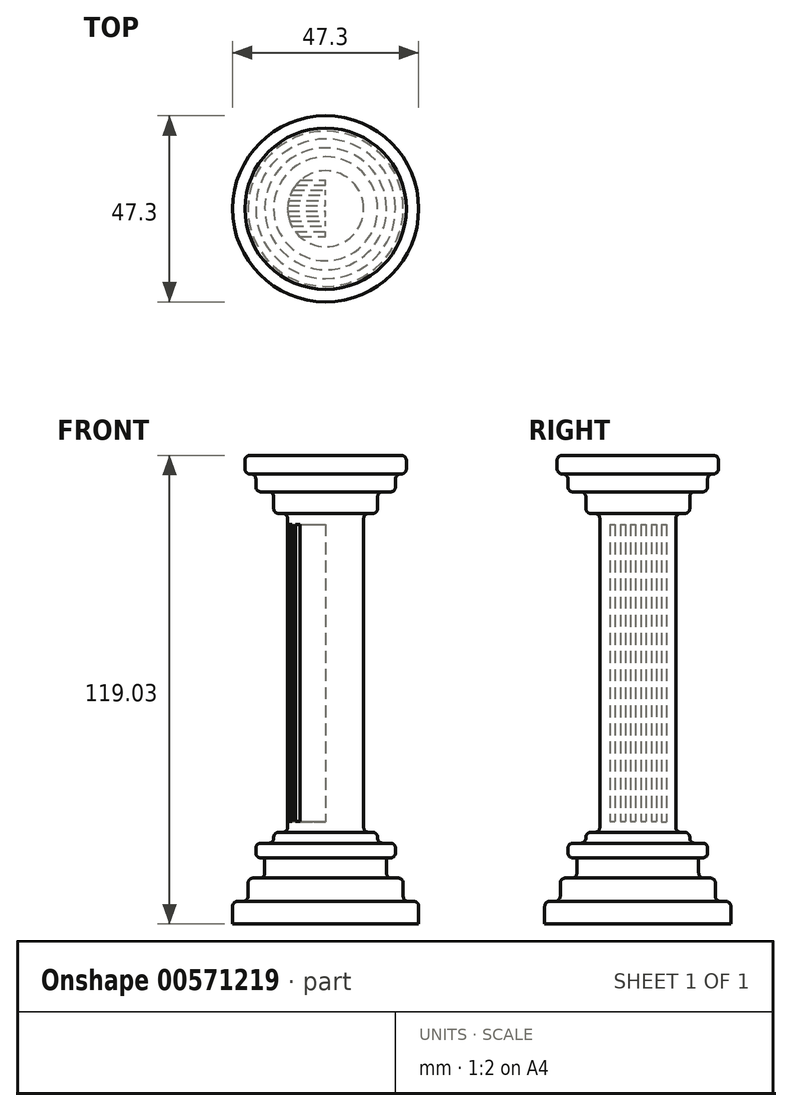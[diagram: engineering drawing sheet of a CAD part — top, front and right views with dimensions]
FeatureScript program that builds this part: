
annotation { "Feature Type Name" : "Feature", "Feature Type Description" : "" }
export const myFeature = defineFeature(function(context is Context, id is Id, definition is map)
    precondition{}
    {
        {
            var Q0;
            Q0=qCreatedBy(makeId("Right.planeOp"),FACE);
            var sketch = newSketch(context, id + "F0", { "sketchPlane" : qUnion([Q0])});
            skLineSegment(sketch, "E0", {"start": v(0, -56.36) * mm, "end": v(0, 43.27) * mm});
            skLineSegment(sketch, "E1", {"start": v(-12.7, 55.97) * mm, "end": v(-19.23, 55.97) * mm});
            skLineSegment(sketch, "E2", {"start": v(-20.5, 54.7) * mm, "end": v(-20.5, 52.5) * mm});
            skLineSegment(sketch, "E3", {"start": v(-19.23, 51.24) * mm, "end": v(-19, 51.24) * mm});
            skLineSegment(sketch, "E4", {"start": v(-17.74, 49.97) * mm, "end": v(-17.74, 47.98) * mm});
            skLineSegment(sketch, "E5", {"start": v(-16.47, 46.7) * mm, "end": v(-14.47, 46.7) * mm});
            skLineSegment(sketch, "E6", {"start": v(-13.2, 45.44) * mm, "end": v(-13.2, 42.46) * mm});
            skLineSegment(sketch, "E7", {"start": v(-11.93, 41.19) * mm, "end": v(-10.93, 41.19) * mm});
            skLineSegment(sketch, "E8", {"start": v(-9.66, 39.92) * mm, "end": v(-9.66, -38.54) * mm});
            skLineSegment(sketch, "E9", {"start": v(-10.93, -39.8) * mm, "end": v(-11.93, -39.8) * mm});
            skLineSegment(sketch, "E10", {"start": v(-13.2, -41.08) * mm, "end": v(-13.2, -41.3) * mm});
            skLineSegment(sketch, "E11", {"start": v(-14.47, -42.57) * mm, "end": v(-16.47, -42.57) * mm});
            skLineSegment(sketch, "E12", {"start": v(-17.74, -43.84) * mm, "end": v(-17.74, -45.04) * mm});
            skLineSegment(sketch, "E13", {"start": v(-16.47, -46.31) * mm, "end": v(-15.47, -46.31) * mm});
            skPoint(sketch, "E13.endSnap0", {"position": v(-15.47, -42.57) * mm});
            skLineSegment(sketch, "E14", {"start": v(-15.47, -46.31) * mm, "end": v(-15.47, -50.17) * mm});
            skLineSegment(sketch, "E15", {"start": v(-16.74, -51.44) * mm, "end": v(-18.44, -51.44) * mm});
            skLineSegment(sketch, "E16", {"start": v(-19.7, -52.7) * mm, "end": v(-19.7, -56.08) * mm});
            skLineSegment(sketch, "E17", {"start": v(-20.98, -57.35) * mm, "end": v(-22.38, -57.35) * mm});
            skLineSegment(sketch, "E18", {"start": v(-23.65, -58.62) * mm, "end": v(-23.65, -63.06) * mm});
            skLineSegment(sketch, "E19", {"start": v(-23.65, -63.06) * mm, "end": v(0, -63.06) * mm});
            skLineSegment(sketch, "E20", {"start": v(0, -63.06) * mm, "end": v(0, -56.36) * mm});
            skPoint(sketch, "E21.visualSharp", {"position": v(0, 55.97) * mm});
            skPoint(sketch, "E22.visualSharp", {"position": v(-20.5, 55.97) * mm});
            skArc(sketch, "E22.filletArc", {"start": v(-19.23, 55.97) * mm, "mid": v(-20.12, 55.6) * mm, "end": v(-20.5, 54.7) * mm});
            skPoint(sketch, "E23.visualSharp", {"position": v(-20.5, 51.24) * mm});
            skArc(sketch, "E23.filletArc", {"start": v(-20.5, 52.5) * mm, "mid": v(-20.12, 51.6) * mm, "end": v(-19.23, 51.24) * mm});
            skPoint(sketch, "E24.visualSharp", {"position": v(-17.74, 51.24) * mm});
            skArc(sketch, "E24.filletArc", {"start": v(-17.74, 49.97) * mm, "mid": v(-18.1, 50.87) * mm, "end": v(-19, 51.24) * mm});
            skPoint(sketch, "E25.visualSharp", {"position": v(-17.74, 46.7) * mm});
            skArc(sketch, "E25.filletArc", {"start": v(-17.74, 47.98) * mm, "mid": v(-17.36, 47.08) * mm, "end": v(-16.47, 46.7) * mm});
            skPoint(sketch, "E26.visualSharp", {"position": v(-13.2, 46.7) * mm});
            skArc(sketch, "E26.filletArc", {"start": v(-13.2, 45.44) * mm, "mid": v(-13.58, 46.33) * mm, "end": v(-14.47, 46.7) * mm});
            skPoint(sketch, "E27.visualSharp", {"position": v(-13.2, 41.19) * mm});
            skArc(sketch, "E27.filletArc", {"start": v(-13.2, 42.46) * mm, "mid": v(-12.83, 41.56) * mm, "end": v(-11.93, 41.19) * mm});
            skPoint(sketch, "E28.visualSharp", {"position": v(-9.66, 41.19) * mm});
            skArc(sketch, "E28.filletArc", {"start": v(-9.66, 39.92) * mm, "mid": v(-10.03, 40.82) * mm, "end": v(-10.93, 41.19) * mm});
            skPoint(sketch, "E29.visualSharp", {"position": v(-9.66, -39.8) * mm});
            skArc(sketch, "E29.filletArc", {"start": v(-10.93, -39.8) * mm, "mid": v(-10.03, -39.44) * mm, "end": v(-9.66, -38.54) * mm});
            skPoint(sketch, "E30.visualSharp", {"position": v(-13.2, -39.8) * mm});
            skArc(sketch, "E30.filletArc", {"start": v(-11.93, -39.8) * mm, "mid": v(-12.83, -40.18) * mm, "end": v(-13.2, -41.08) * mm});
            skPoint(sketch, "E31.visualSharp", {"position": v(-13.2, -42.57) * mm});
            skArc(sketch, "E31.filletArc", {"start": v(-14.47, -42.57) * mm, "mid": v(-13.58, -42.2) * mm, "end": v(-13.2, -41.3) * mm});
            skPoint(sketch, "E32.visualSharp", {"position": v(-17.74, -42.57) * mm});
            skArc(sketch, "E32.filletArc", {"start": v(-16.47, -42.57) * mm, "mid": v(-17.36, -42.94) * mm, "end": v(-17.74, -43.84) * mm});
            skPoint(sketch, "E33.visualSharp", {"position": v(-17.74, -46.31) * mm});
            skArc(sketch, "E33.filletArc", {"start": v(-17.74, -45.04) * mm, "mid": v(-17.36, -45.94) * mm, "end": v(-16.47, -46.31) * mm});
            skPoint(sketch, "E34.visualSharp", {"position": v(-15.47, -51.44) * mm});
            skArc(sketch, "E34.filletArc", {"start": v(-16.74, -51.44) * mm, "mid": v(-15.84, -51.06) * mm, "end": v(-15.47, -50.17) * mm});
            skPoint(sketch, "E35.visualSharp", {"position": v(-19.7, -51.44) * mm});
            skArc(sketch, "E35.filletArc", {"start": v(-18.44, -51.44) * mm, "mid": v(-19.33, -51.8) * mm, "end": v(-19.7, -52.7) * mm});
            skPoint(sketch, "E36.visualSharp", {"position": v(-19.7, -57.35) * mm});
            skArc(sketch, "E36.filletArc", {"start": v(-20.98, -57.35) * mm, "mid": v(-20.08, -56.98) * mm, "end": v(-19.7, -56.08) * mm});
            skPoint(sketch, "E37.visualSharp", {"position": v(-23.65, -57.35) * mm});
            skArc(sketch, "E37.filletArc", {"start": v(-22.38, -57.35) * mm, "mid": v(-23.28, -57.72) * mm, "end": v(-23.65, -58.62) * mm});
            skLineSegment(sketch, "E38", {"start": v(-12.7, 55.97) * mm, "end": v(0, 55.97) * mm});
            skLineSegment(sketch, "E39", {"start": v(0, 43.27) * mm, "end": v(0, 55.97) * mm});
            skSolve(sketch);
        }
        {
            var Q0;
            Q0=makeQuery(id+"F0.imprint","IMPRINT",FACE,{"disambiguationData":[TD([[makeQuery(id+"F0.imprint","IMPRINT",EDGE,{"derivedFrom":sQuery(id+"F0.wireOp",EDGE,"E0")}),1.0]])]});
            var Q1;
            Q1=sQuery(id+"F0.wireOp",EDGE,"E0");
            revolve(context, id + "F1", {"entities" : qUnion([Q0]), "axis" : qUnion([Q1]), "revolveType" : RevolveType.FULL});
        }
        {
            var Q0;
            Q0=qCreatedBy(makeId("Right.planeOp"),FACE);
            var sketch = newSketch(context, id + "F2", { "sketchPlane" : qUnion([Q0])});
            skLineSegment(sketch, "E40.bottom", {"start": v(-7.1, 38.43) * mm, "end": v(-5.8, 38.43) * mm});
            skLineSegment(sketch, "E40.top", {"start": v(-7.1, -37.05) * mm, "end": v(-5.8, -37.05) * mm});
            skLineSegment(sketch, "E40.left", {"start": v(-7.1, 38.43) * mm, "end": v(-7.1, -37.05) * mm});
            skLineSegment(sketch, "E40.right", {"start": v(-5.8, 38.43) * mm, "end": v(-5.8, -37.05) * mm});
            skLineSegment(sketch, "E41.bottom", {"start": v(-4.38, 38.43) * mm, "end": v(-3.1, 38.43) * mm});
            skLineSegment(sketch, "E41.top", {"start": v(-4.38, -37.08) * mm, "end": v(-3.1, -37.08) * mm});
            skLineSegment(sketch, "E41.left", {"start": v(-4.38, 38.43) * mm, "end": v(-4.38, -37.08) * mm});
            skLineSegment(sketch, "E41.right", {"start": v(-3.1, 38.43) * mm, "end": v(-3.1, -37.08) * mm});
            skLineSegment(sketch, "E42.bottom", {"start": v(-1.87, 38.42) * mm, "end": v(-0.59, 38.42) * mm});
            skLineSegment(sketch, "E42.top", {"start": v(-1.87, -37.07) * mm, "end": v(-0.59, -37.07) * mm});
            skLineSegment(sketch, "E42.left", {"start": v(-1.87, 38.42) * mm, "end": v(-1.87, -37.07) * mm});
            skLineSegment(sketch, "E42.right", {"start": v(-0.59, 38.42) * mm, "end": v(-0.59, -37.07) * mm});
            skLineSegment(sketch, "E43.bottom", {"start": v(0.78, 38.42) * mm, "end": v(2.07, 38.42) * mm});
            skLineSegment(sketch, "E43.top", {"start": v(0.78, -37.08) * mm, "end": v(2.07, -37.08) * mm});
            skLineSegment(sketch, "E43.left", {"start": v(0.78, 38.42) * mm, "end": v(0.78, -37.08) * mm});
            skLineSegment(sketch, "E43.right", {"start": v(2.07, 38.42) * mm, "end": v(2.07, -37.08) * mm});
            skLineSegment(sketch, "E44.bottom", {"start": v(3.49, 38.45) * mm, "end": v(4.77, 38.45) * mm});
            skLineSegment(sketch, "E44.top", {"start": v(3.49, -37.07) * mm, "end": v(4.77, -37.07) * mm});
            skLineSegment(sketch, "E44.left", {"start": v(3.49, 38.45) * mm, "end": v(3.49, -37.07) * mm});
            skLineSegment(sketch, "E44.right", {"start": v(4.77, 38.45) * mm, "end": v(4.77, -37.07) * mm});
            skLineSegment(sketch, "E45.bottom", {"start": v(6, 38.44) * mm, "end": v(7.29, 38.44) * mm});
            skLineSegment(sketch, "E45.top", {"start": v(6, -37.1) * mm, "end": v(7.29, -37.1) * mm});
            skLineSegment(sketch, "E45.left", {"start": v(6, 38.44) * mm, "end": v(6, -37.1) * mm});
            skLineSegment(sketch, "E45.right", {"start": v(7.29, 38.44) * mm, "end": v(7.29, -37.1) * mm});
            skSolve(sketch);
        }
        {
            var Q0;
            Q0 = qSketchRegion(id + "F2", true);
            extrude(context, id + "F3", {"entities" : qUnion([Q0]), "operationType" : NewBodyOperationType.REMOVE, "oppositeDirection" : true, "depth" : 21.08 * mm, "offsetDistance" : 25.4 * mm});
        }
    });
